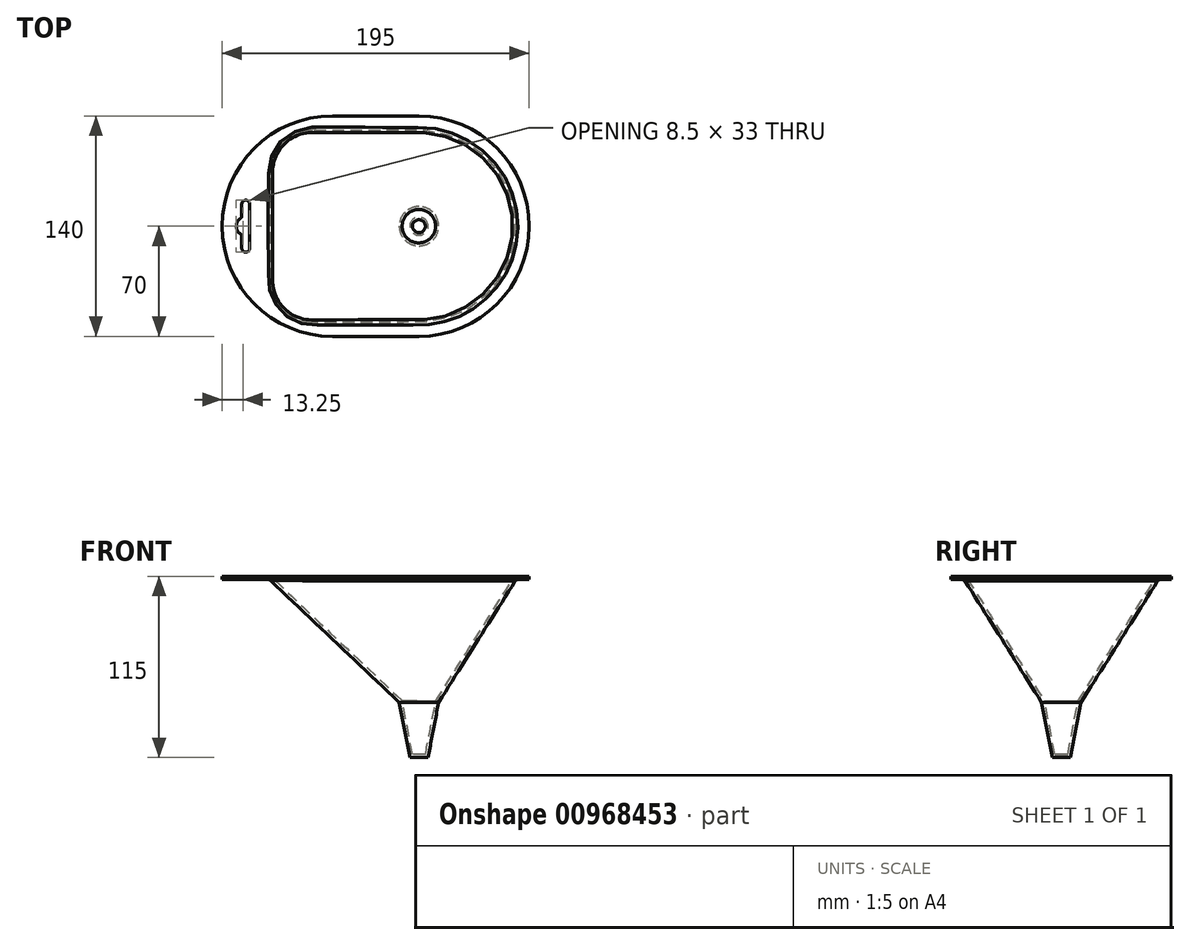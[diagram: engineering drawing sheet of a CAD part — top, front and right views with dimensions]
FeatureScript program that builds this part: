
annotation { "Feature Type Name" : "Feature", "Feature Type Description" : "" }
export const myFeature = defineFeature(function(context is Context, id is Id, definition is map)
    precondition{}
    {
        {
            var Q0;
            Q0=qCreatedBy(makeId("Top.planeOp"),FACE);
            cPlane(context, id + "F0", {"entities" : qUnion([Q0]), "cplaneType" : CPlaneType.OFFSET, "offset" : 80 * mm, "oppositeDirection" : true, "width" : 150 * mm, "height" : 150 * mm});
        }
        {
            var Q0;
            Q0=qCreatedBy(id+"F0.planeOp",FACE);
            cPlane(context, id + "F1", {"entities" : qUnion([Q0]), "cplaneType" : CPlaneType.OFFSET, "offset" : 35 * mm, "oppositeDirection" : true, "width" : 150 * mm, "height" : 150 * mm});
        }
        {
            var Q0;
            Q0=qCreatedBy(makeId("Top.planeOp"),FACE);
            var sketch = newSketch(context, id + "F2", { "sketchPlane" : qUnion([Q0])});
            skCircle(sketch, "E0", {"center": v(0, 0) * mm, "radius": 5.75 * mm});
            skCircle(sketch, "E1", {"center": v(0, 0) * mm, "radius": 12.5 * mm});
            skArc(sketch, "E2", {"start": v(0, -70) * mm, "mid": v(70, 0) * mm, "end": v(0, 70) * mm});
            skArc(sketch, "E3", {"start": v(-55, 70) * mm, "mid": v(-125, 0) * mm, "end": v(-55, -70) * mm});
            skLineSegment(sketch, "E4", {"start": v(-55, 70) * mm, "end": v(0, 70) * mm});
            skLineSegment(sketch, "E5", {"start": v(-55, -70) * mm, "end": v(0, -70) * mm});
            skLineSegment(sketch, "E6", {"start": v(-97, 35) * mm, "end": v(-97, -35) * mm});
            skLineSegment(sketch, "E7", {"start": v(-69, 63) * mm, "end": v(0, 63) * mm});
            skLineSegment(sketch, "E8", {"start": v(-69, -63) * mm, "end": v(0, -63) * mm});
            skArc(sketch, "E9", {"start": v(0, -63) * mm, "mid": v(63, 0) * mm, "end": v(0, 63) * mm});
            skPoint(sketch, "E10.visualSharp", {"position": v(-97, 63) * mm});
            skArc(sketch, "E10.filletArc", {"start": v(-69, 63) * mm, "mid": v(-88.8, 54.8) * mm, "end": v(-97, 35) * mm});
            skPoint(sketch, "E11.visualSharp", {"position": v(-97, -63) * mm});
            skArc(sketch, "E11.filletArc", {"start": v(-97, -35) * mm, "mid": v(-88.8, -54.8) * mm, "end": v(-69, -63) * mm});
            skArc(sketch, "E12", {"start": v(-107.5, 14) * mm, "mid": v(-110, 16.5) * mm, "end": v(-112.5, 14) * mm});
            skLineSegment(sketch, "E13", {"start": v(-110, 14) * mm, "end": v(-110, -14) * mm, "construction": true});
            skArc(sketch, "E14", {"start": v(-112.5, -14) * mm, "mid": v(-110, -16.5) * mm, "end": v(-107.5, -14) * mm});
            skLineSegment(sketch, "E15", {"start": v(-107.5, 14) * mm, "end": v(-107.5, -14) * mm});
            skArc(sketch, "E16", {"start": v(-113.38, 4.96) * mm, "mid": v(-116, 0) * mm, "end": v(-113.37, -4.96) * mm});
            skLineSegment(sketch, "E17", {"start": v(-112.5, 14) * mm, "end": v(-112.5, 6.61) * mm});
            skLineSegment(sketch, "E18", {"start": v(-112.5, -14) * mm, "end": v(-112.5, -6.61) * mm});
            skPoint(sketch, "E19.visualSharp", {"position": v(-112.5, 5.45) * mm});
            skArc(sketch, "E19.filletArc", {"start": v(-113.38, 4.96) * mm, "mid": v(-112.73, 5.68) * mm, "end": v(-112.5, 6.61) * mm});
            skPoint(sketch, "E20.visualSharp", {"position": v(-112.5, -5.45) * mm});
            skArc(sketch, "E20.filletArc", {"start": v(-112.5, -6.61) * mm, "mid": v(-112.73, -5.68) * mm, "end": v(-113.37, -4.96) * mm});
            skSolve(sketch);
        }
        {
            var Q0;
            Q0=qCreatedBy(makeId("Top.planeOp"),FACE);
            var sketch = newSketch(context, id + "F3", { "sketchPlane" : qUnion([Q0])});
            skArc(sketch, "E21.0", {"start": v(-69, 63) * mm, "mid": v(-88.8, 54.8) * mm, "end": v(-97, 35) * mm});
            skLineSegment(sketch, "E21.1", {"start": v(-69, 63) * mm, "end": v(0, 63) * mm});
            skArc(sketch, "E21.2", {"start": v(0, -63) * mm, "mid": v(63, 0) * mm, "end": v(0, 63) * mm});
            skLineSegment(sketch, "E21.3", {"start": v(-69, -63) * mm, "end": v(0, -63) * mm});
            skArc(sketch, "E21.4", {"start": v(-97, -35) * mm, "mid": v(-88.8, -54.8) * mm, "end": v(-69, -63) * mm});
            skLineSegment(sketch, "E21.5", {"start": v(-97, 35) * mm, "end": v(-97, -35) * mm});
            skPoint(sketch, "E22", {"position": v(-97, 0) * mm});
            skSolve(sketch);
        }
        {
            var Q0;
            Q0=qCreatedBy(id+"F0.planeOp",FACE);
            var sketch = newSketch(context, id + "F4", { "sketchPlane" : qUnion([Q0])});
            skCircle(sketch, "E23.0", {"center": v(0, 0) * mm, "radius": 12.5 * mm});
            skPoint(sketch, "E24", {"position": v(-12.5, 0) * mm});
            skSolve(sketch);
        }
        {
            var Q0;
            Q0=qCreatedBy(id+"F1.planeOp",FACE);
            var sketch = newSketch(context, id + "F5", { "sketchPlane" : qUnion([Q0])});
            skCircle(sketch, "E25.0", {"center": v(0, 0) * mm, "radius": 5.75 * mm});
            skSolve(sketch);
        }
        {
            var Q0;
            Q0=qCreatedBy(makeId("Front.planeOp"),FACE);
            var sketch = newSketch(context, id + "F6", { "sketchPlane" : qUnion([Q0])});
            skLineSegment(sketch, "E26", {"start": v(-97, 0) * mm, "end": v(-12.5, -80) * mm});
            skLineSegment(sketch, "E27", {"start": v(-12.5, -80) * mm, "end": v(-5.75, -115) * mm});
            skLineSegment(sketch, "E28", {"start": v(63, 0) * mm, "end": v(12.5, -80) * mm});
            skLineSegment(sketch, "E29", {"start": v(12.5, -80) * mm, "end": v(5.75, -115) * mm});
            skSolve(sketch);
        }
        {
            var Q0;
            Q0=makeQuery(id+"F3.imprint","IMPRINT",FACE,{"disambiguationData":[TD([[makeQuery(id+"F3.imprint","IMPRINT",EDGE,{"derivedFrom":sQuery(id+"F3.wireOp",EDGE,"E21.0")}),1.0]])]});
            var Q1;
            Q1=makeQuery(id+"F4.imprint","IMPRINT",FACE,{"disambiguationData":[TD([[makeQuery(id+"F4.imprint","IMPRINT",EDGE,{"derivedFrom":sQuery(id+"F4.wireOp",EDGE,"E23.0")}),1.0]])]});
            var Q2;
            Q2=sQuery(id+"F6.wireOp",EDGE,"E26");
            var Q3;
            Q3=sQuery(id+"F6.wireOp",EDGE,"E28");
            loft(context, id + "F7", {"addGuides" : true, "sheetProfilesArray" : [{ "sheetProfileEntities" : qUnion([Q0]) }, { "sheetProfileEntities" : qUnion([Q1]) }], "guidesArray" : [{ "guideEntities" : qUnion([Q2]), "guideDerivativeType" : LoftGuideDerivativeType.DEFAULT, "guideDerivativeMagnitude" : 1 }, { "guideEntities" : qUnion([Q3]), "guideDerivativeType" : LoftGuideDerivativeType.DEFAULT, "guideDerivativeMagnitude" : 1 }]});
        }
        {
            var Q1;
            Q1 = qSketchRegion(id + "F4", true);
            var Q2;
            Q2 = qSketchRegion(id + "F5", true);
            loft(context, id + "F8", {"operationType" : NewBodyOperationType.ADD, "sheetProfilesArray" : [{ "sheetProfileEntities" : qUnion([Q1]) }, { "sheetProfileEntities" : qUnion([Q2]) }]});
        }
        {
            var Q0;
            Q0=makeQuery(id+"F2.imprint","IMPRINT",FACE,{"disambiguationData":[TD([[makeQuery(id+"F2.imprint","IMPRINT",EDGE,{"derivedFrom":sQuery(id+"F2.wireOp",EDGE,"E2")}),1.0]])]});
            var Q1;
            Q1=makeQuery(id+"F2.imprint","IMPRINT",FACE,{"disambiguationData":[TD([[makeQuery(id+"F2.imprint","IMPRINT",EDGE,{"derivedFrom":sQuery(id+"F2.wireOp",EDGE,"E1")}),-1.0]])]});
            extrude(context, id + "F9", {"entities" : qUnion([Q0, Q1]), "operationType" : NewBodyOperationType.ADD, "oppositeDirection" : true, "depth" : 2 * mm, "offsetDistance" : 25 * mm});
        }
        {
            var Q0;
            Q0=makeQuery(id+"F9.boolean.opBoolean","INTERSECT",EDGE,{"derivedFrom":[makeQuery(id+"F7.opLoft","SWEPT_FACE",FACE,{"disambiguationData":[OSD([sQuery(id+"F3.wireOp",EDGE,"E21.0"),sQuery(id+"F3.wireOp",EDGE,"E21.1"),sQuery(id+"F3.wireOp",EDGE,"E21.2"),sQuery(id+"F3.wireOp",EDGE,"E21.3"),sQuery(id+"F3.wireOp",EDGE,"E21.4"),sQuery(id+"F3.wireOp",EDGE,"E21.5"),sQuery(id+"F4.wireOp",EDGE,"E23.0"),sQuery(id+"F6.wireOp",VERTEX,"E26.start"),sQuery(id+"F6.wireOp",VERTEX,"E26.end"),sQuery(id+"F6.wireOp",VERTEX,"E28.start"),sQuery(id+"F6.wireOp",VERTEX,"E28.end"),sQuery(id+"F6.wireOp",EDGE,"E26"),sQuery(id+"F6.wireOp",EDGE,"E28")])]}),makeQuery(id+"F9.opExtrude","CAP_FACE",FACE,{"disambiguationData":[OSD([sQuery(id+"F2.wireOp",EDGE,"E1"),sQuery(id+"F2.wireOp",EDGE,"E2"),sQuery(id+"F2.wireOp",EDGE,"E3"),sQuery(id+"F2.wireOp",EDGE,"E4"),sQuery(id+"F2.wireOp",EDGE,"E5"),sQuery(id+"F2.wireOp",EDGE,"E12"),sQuery(id+"F2.wireOp",EDGE,"E14"),sQuery(id+"F2.wireOp",EDGE,"E15"),sQuery(id+"F2.wireOp",EDGE,"E16"),sQuery(id+"F2.wireOp",EDGE,"E17"),sQuery(id+"F2.wireOp",EDGE,"E18"),sQuery(id+"F2.wireOp",EDGE,"E19.filletArc"),sQuery(id+"F2.wireOp",EDGE,"E20.filletArc")])],"isStart":false})]});
            fillet(context, id + "F10", {"entities" : qUnion([Q0]), "radius" : 2 * mm, "tangentPropagation" : true, "allowEdgeOverflow" : false});
        }
        {
            var Q0;
            Q0=makeQuery(id+"F9.boolean.opBoolean","MERGE",FACE,{"derivedFrom":[makeQuery(id+"F7.opLoft","CAP_FACE",FACE,{"disambiguationData":[OSD([makeQuery(id+"F3.imprint","IMPRINT",FACE,{"disambiguationData":[TD([[makeQuery(id+"F3.imprint","IMPRINT",EDGE,{"derivedFrom":sQuery(id+"F3.wireOp",EDGE,"E21.0")}),1.0]])]})])],"isStart":true}),makeQuery(id+"F9.opExtrude","CAP_FACE",FACE,{"disambiguationData":[OSD([sQuery(id+"F2.wireOp",EDGE,"E1"),sQuery(id+"F2.wireOp",EDGE,"E2"),sQuery(id+"F2.wireOp",EDGE,"E3"),sQuery(id+"F2.wireOp",EDGE,"E4"),sQuery(id+"F2.wireOp",EDGE,"E5"),sQuery(id+"F2.wireOp",EDGE,"E12"),sQuery(id+"F2.wireOp",EDGE,"E14"),sQuery(id+"F2.wireOp",EDGE,"E15"),sQuery(id+"F2.wireOp",EDGE,"E16"),sQuery(id+"F2.wireOp",EDGE,"E17"),sQuery(id+"F2.wireOp",EDGE,"E18"),sQuery(id+"F2.wireOp",EDGE,"E19.filletArc"),sQuery(id+"F2.wireOp",EDGE,"E20.filletArc")])],"isStart":true})]});
            var Q1;
            Q1=makeQuery(id+"F8.opLoft","CAP_FACE",FACE,{"disambiguationData":[OSD([makeQuery(id+"F5.imprint","IMPRINT",FACE,{"disambiguationData":[TD([[makeQuery(id+"F5.imprint","IMPRINT",EDGE,{"derivedFrom":sQuery(id+"F5.wireOp",EDGE,"E25.0")}),1.0]])]})])],"isStart":true});
            shell(context, id + "F11", {"entities" : qUnion([Q0, Q1]), "thickness" : 2 * mm});
        }
    });
